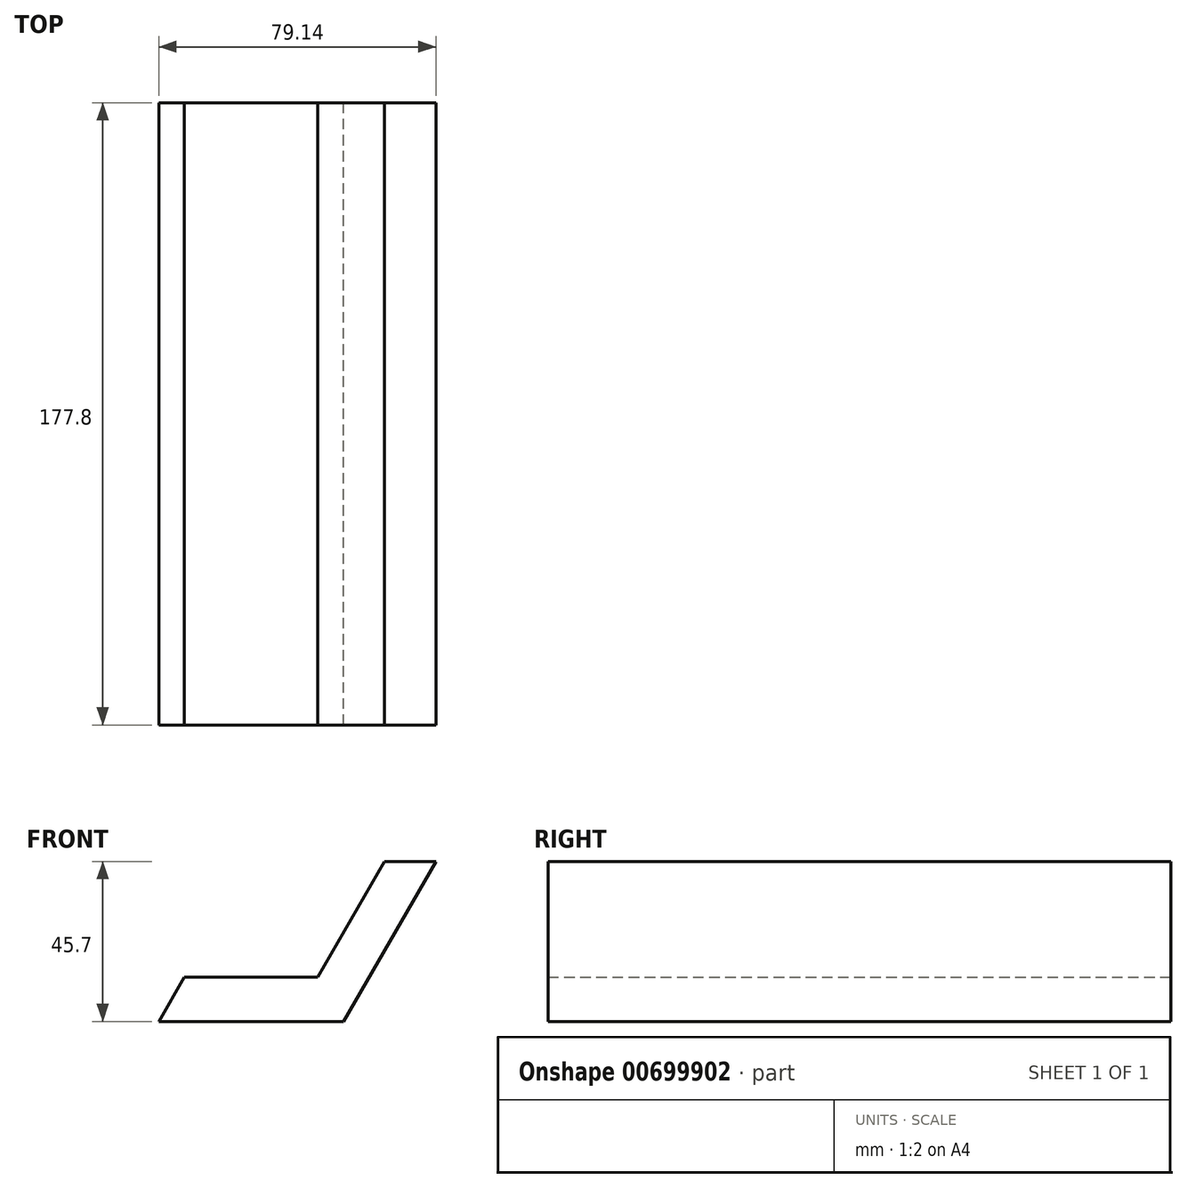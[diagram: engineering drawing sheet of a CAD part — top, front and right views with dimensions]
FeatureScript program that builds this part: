
annotation { "Feature Type Name" : "Feature", "Feature Type Description" : "" }
export const myFeature = defineFeature(function(context is Context, id is Id, definition is map)
    precondition{}
    {
        {
            var Q0;
            Q0=qCreatedBy(makeId("Front.planeOp"),FACE);
            var sketch = newSketch(context, id + "F0", { "sketchPlane" : qUnion([Q0])});
            skLineSegment(sketch, "E0", {"start": v(-41.82, 24.06) * mm, "end": v(-3.72, 24.06) * mm});
            skLineSegment(sketch, "E1", {"start": v(-41.82, 24.06) * mm, "end": v(-49.15, 11.36) * mm});
            skLineSegment(sketch, "E2", {"start": v(-49.15, 11.36) * mm, "end": v(3.61, 11.36) * mm});
            skLineSegment(sketch, "E3", {"start": v(-3.72, 24.06) * mm, "end": v(15.33, 57.06) * mm});
            skLineSegment(sketch, "E4", {"start": v(15.33, 57.06) * mm, "end": v(30, 57.06) * mm});
            skLineSegment(sketch, "E5", {"start": v(3.61, 11.36) * mm, "end": v(30, 57.06) * mm});
            skLineSegment(sketch, "E6.0", {"start": v(3.61, 11.36) * mm, "end": v(30, 57.06) * mm, "construction": true});
            skSolve(sketch);
        }
        {
            var Q0;
            Q0=makeQuery(id+"F0.imprint","IMPRINT",FACE,{"disambiguationData":[TD([[makeQuery(id+"F0.imprint","IMPRINT",EDGE,{"derivedFrom":sQuery(id+"F0.wireOp",EDGE,"E0")}),-1.0]])]});
            extrude(context, id + "F1", {"entities" : qUnion([Q0]), "depth" : 177.8 * mm, "offsetDistance" : 25.4 * mm});
        }
    });
